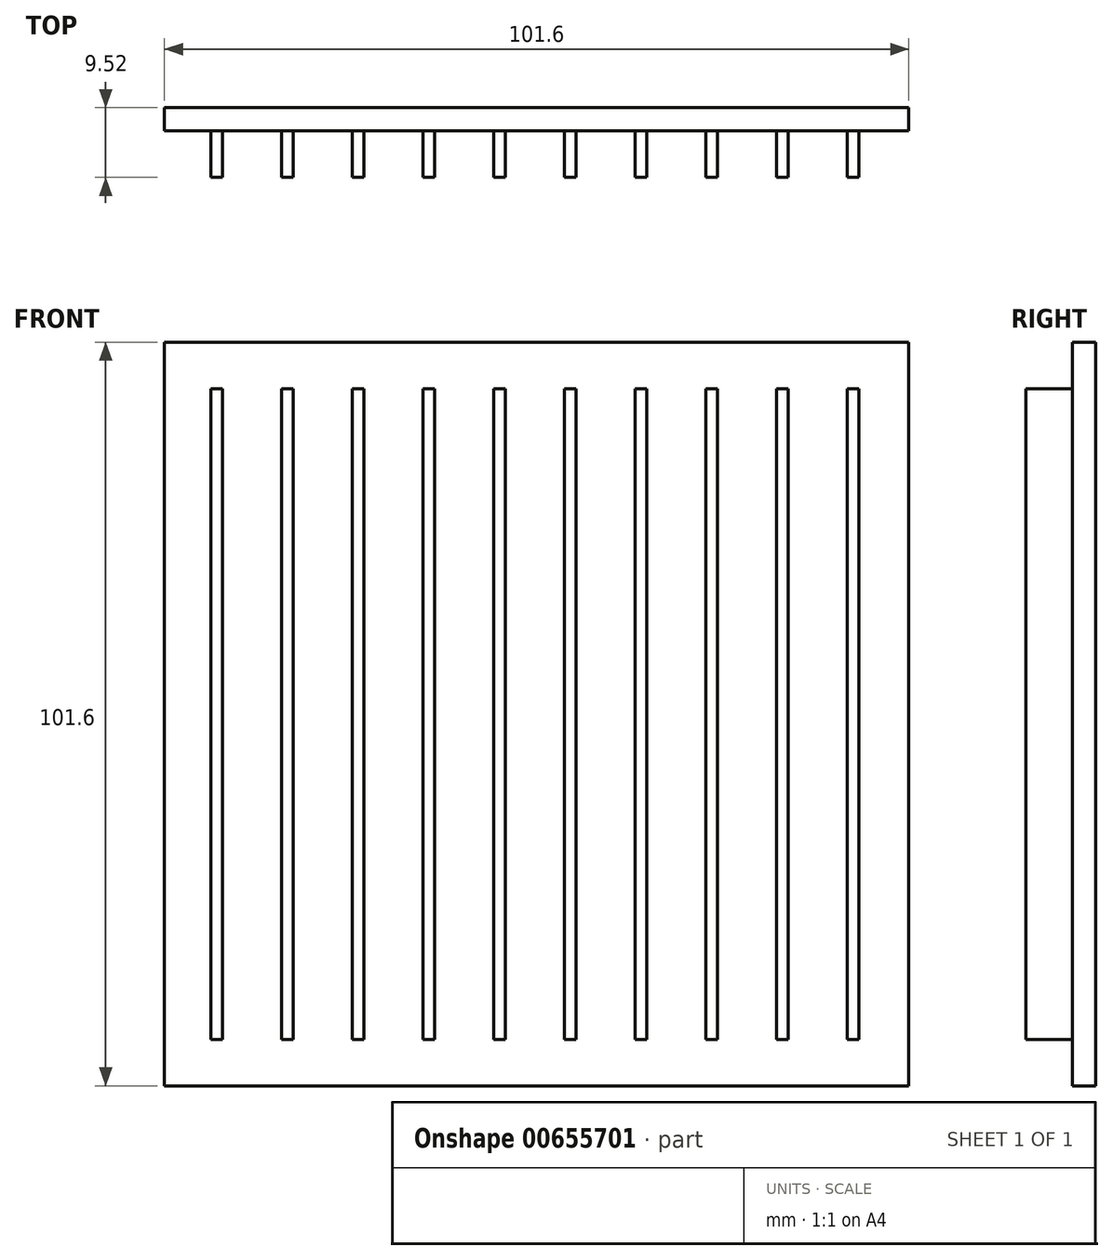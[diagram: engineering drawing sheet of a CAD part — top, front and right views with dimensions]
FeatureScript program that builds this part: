
annotation { "Feature Type Name" : "Feature", "Feature Type Description" : "" }
export const myFeature = defineFeature(function(context is Context, id is Id, definition is map)
    precondition{}
    {
        {
            var Q0;
            Q0=qCreatedBy(makeId("Front.planeOp"),FACE);
            var sketch = newSketch(context, id + "F0", { "sketchPlane" : qUnion([Q0])});
            skLineSegment(sketch, "E0.bottom", {"start": v(50.8, -50.8) * mm, "end": v(-50.8, -50.8) * mm});
            skLineSegment(sketch, "E0.top", {"start": v(50.8, 50.8) * mm, "end": v(-50.8, 50.8) * mm});
            skLineSegment(sketch, "E0.left", {"start": v(50.8, -50.8) * mm, "end": v(50.8, 50.8) * mm});
            skLineSegment(sketch, "E0.right", {"start": v(-50.8, -50.8) * mm, "end": v(-50.8, 50.8) * mm});
            skPoint(sketch, "E0.middle", {"position": v(0, 0) * mm});
            skSolve(sketch);
        }
        {
            var Q0;
            Q0 = qSketchRegion(id + "F0", true);
            extrude(context, id + "F1", {"entities" : qUnion([Q0]), "oppositeDirection" : true, "depth" : 3.17 * mm, "offsetDistance" : 25.4 * mm});
        }
        {
            var Q0;
            Q0=makeQuery(id+"F1.opExtrude","CAP_FACE",FACE,{"disambiguationData":[OSD([sQuery(id+"F0.wireOp",EDGE,"E0.bottom"),sQuery(id+"F0.wireOp",EDGE,"E0.top"),sQuery(id+"F0.wireOp",EDGE,"E0.left"),sQuery(id+"F0.wireOp",EDGE,"E0.right")])],"isStart":true});
            var sketch = newSketch(context, id + "F2", { "sketchPlane" : qUnion([Q0])});
            skLineSegment(sketch, "E1.left", {"start": v(44.45, -44.45) * mm, "end": v(44.45, 44.45) * mm});
            skLineSegment(sketch, "E1.right", {"start": v(-44.45, -44.45) * mm, "end": v(-44.45, 44.45) * mm});
            skPoint(sketch, "E1.middle", {"position": v(0, 0) * mm});
            skLineSegment(sketch, "E2.bottom", {"start": v(-44.45, 44.45) * mm, "end": v(-42.86, 44.45) * mm});
            skLineSegment(sketch, "E2.top", {"start": v(-44.45, -44.45) * mm, "end": v(-42.86, -44.45) * mm});
            skLineSegment(sketch, "E2.right", {"start": v(-42.86, 44.45) * mm, "end": v(-42.86, -44.45) * mm});
            skLineSegment(sketch, "E3.1.0.0", {"start": v(-34.8, -44.45) * mm, "end": v(-34.8, 44.45) * mm});
            skLineSegment(sketch, "E3.1.0.1", {"start": v(-34.8, 44.45) * mm, "end": v(-33.21, 44.45) * mm});
            skLineSegment(sketch, "E3.1.0.2", {"start": v(-33.21, 44.45) * mm, "end": v(-33.21, -44.45) * mm});
            skLineSegment(sketch, "E3.1.0.3", {"start": v(-34.8, -44.45) * mm, "end": v(-33.21, -44.45) * mm});
            skLineSegment(sketch, "E3.2.0.0", {"start": v(-25.15, -44.45) * mm, "end": v(-25.15, 44.45) * mm});
            skLineSegment(sketch, "E3.2.0.1", {"start": v(-25.15, 44.45) * mm, "end": v(-23.56, 44.45) * mm});
            skLineSegment(sketch, "E3.2.0.2", {"start": v(-23.56, 44.45) * mm, "end": v(-23.56, -44.45) * mm});
            skLineSegment(sketch, "E3.2.0.3", {"start": v(-25.15, -44.45) * mm, "end": v(-23.56, -44.45) * mm});
            skLineSegment(sketch, "E3.3.0.0", {"start": v(-15.5, -44.45) * mm, "end": v(-15.5, 44.45) * mm});
            skLineSegment(sketch, "E3.3.0.1", {"start": v(-15.5, 44.45) * mm, "end": v(-13.9, 44.45) * mm});
            skLineSegment(sketch, "E3.3.0.2", {"start": v(-13.9, 44.45) * mm, "end": v(-13.9, -44.45) * mm});
            skLineSegment(sketch, "E3.3.0.3", {"start": v(-15.5, -44.45) * mm, "end": v(-13.9, -44.45) * mm});
            skLineSegment(sketch, "E3.4.0.0", {"start": v(-5.84, -44.45) * mm, "end": v(-5.84, 44.45) * mm});
            skLineSegment(sketch, "E3.4.0.1", {"start": v(-5.84, 44.45) * mm, "end": v(-4.25, 44.45) * mm});
            skLineSegment(sketch, "E3.4.0.2", {"start": v(-4.25, 44.45) * mm, "end": v(-4.25, -44.45) * mm});
            skLineSegment(sketch, "E3.4.0.3", {"start": v(-5.84, -44.45) * mm, "end": v(-4.25, -44.45) * mm});
            skLineSegment(sketch, "E3.5.0.0", {"start": v(3.8, -44.45) * mm, "end": v(3.81, 44.45) * mm});
            skLineSegment(sketch, "E3.5.0.1", {"start": v(3.81, 44.45) * mm, "end": v(5.4, 44.45) * mm});
            skLineSegment(sketch, "E3.5.0.2", {"start": v(5.4, 44.45) * mm, "end": v(5.4, -44.45) * mm});
            skLineSegment(sketch, "E3.5.0.3", {"start": v(3.81, -44.45) * mm, "end": v(5.4, -44.45) * mm});
            skLineSegment(sketch, "E3.6.0.0", {"start": v(13.46, -44.45) * mm, "end": v(13.46, 44.45) * mm});
            skLineSegment(sketch, "E3.6.0.1", {"start": v(13.46, 44.45) * mm, "end": v(15.05, 44.45) * mm});
            skLineSegment(sketch, "E3.6.0.2", {"start": v(15.05, 44.45) * mm, "end": v(15.05, -44.45) * mm});
            skLineSegment(sketch, "E3.6.0.3", {"start": v(13.46, -44.45) * mm, "end": v(15.05, -44.45) * mm});
            skLineSegment(sketch, "E3.7.0.0", {"start": v(23.11, -44.45) * mm, "end": v(23.11, 44.45) * mm});
            skLineSegment(sketch, "E3.7.0.1", {"start": v(23.11, 44.45) * mm, "end": v(24.7, 44.45) * mm});
            skLineSegment(sketch, "E3.7.0.2", {"start": v(24.7, 44.45) * mm, "end": v(24.7, -44.45) * mm});
            skLineSegment(sketch, "E3.7.0.3", {"start": v(23.11, -44.45) * mm, "end": v(24.7, -44.45) * mm});
            skLineSegment(sketch, "E3.8.0.0", {"start": v(32.77, -44.45) * mm, "end": v(32.77, 44.45) * mm});
            skLineSegment(sketch, "E3.8.0.1", {"start": v(32.77, 44.45) * mm, "end": v(34.35, 44.45) * mm});
            skLineSegment(sketch, "E3.8.0.2", {"start": v(34.35, 44.45) * mm, "end": v(34.35, -44.45) * mm});
            skLineSegment(sketch, "E3.8.0.3", {"start": v(32.77, -44.45) * mm, "end": v(34.35, -44.45) * mm});
            skLineSegment(sketch, "E3.9.0.0", {"start": v(42.42, -44.45) * mm, "end": v(42.42, 44.45) * mm});
            skLineSegment(sketch, "E3.9.0.1", {"start": v(42.42, 44.45) * mm, "end": v(44, 44.45) * mm});
            skLineSegment(sketch, "E3.9.0.2", {"start": v(44, 44.45) * mm, "end": v(44, -44.45) * mm});
            skLineSegment(sketch, "E3.9.0.3", {"start": v(42.42, -44.45) * mm, "end": v(44, -44.45) * mm});
            skLineSegment(sketch, "E3.direction1", {"start": v(-44.45, -44.45) * mm, "end": v(-34.8, -44.45) * mm, "construction": true});
            skSolve(sketch);
        }
        {
            var Q0;
            Q0 = qSketchRegion(id + "F2", true);
            extrude(context, id + "F3", {"entities" : qUnion([Q0]), "operationType" : NewBodyOperationType.ADD, "depth" : 6.35 * mm, "offsetDistance" : 25.4 * mm});
        }
    });
